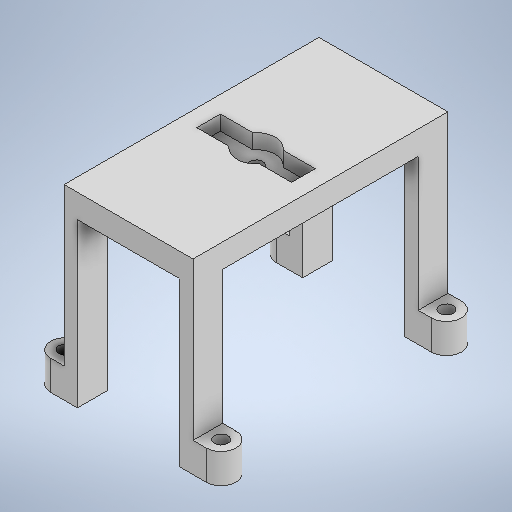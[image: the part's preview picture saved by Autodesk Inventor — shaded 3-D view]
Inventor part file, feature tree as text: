
AUTODESK INVENTOR PART (.ipt)
format: ipt  version: 2025.1 (Build 291241000, 241)  size: 315,392 bytes
history: native  units: in
note: dims shown in document units (in); Inventor stores cm internally (conversion verified against a paired STEP export)
features: extrude x5, sketch x5
ambient origin geometry x8: Origin, YZ Plane, XZ Plane, XY Plane, X Axis, Y Axis, Z Axis, Center Point
bodies: Solid1 (feature_tree)
feature tree (10):
  extrude  "Extrusion1"  Depth=0.3937in
  extrude  "Extrusion2"  Depth=0.3937in
  extrude  "Extrusion3"  Depth=0.3543in
  extrude  "Extrusion4"  Depth=1.7717in TaperAngle=0.0deg
  extrude  "Extrusion5"  Depth=0.315in
  sketch  "Sketch1"  dims[d0=0.3937in d1=0.3937in]
  sketch  "Sketch2"  dims[d2=0.3937in d3=0.3937in]
  sketch  "Sketch3"  dims[d4=0.3543in d5=0.3543in]
  sketch  "Sketch4"  dims[d6=0.3937in d7=0.0in d9=1.7717in d10=0.0in]
  sketch  "Sketch5"  dims[d11=0.315in d12=0.0in d13=0.5118in d14=1.2598in d15=0.315in d16=0.1969in d17=0.0in d18=0.1772in d19=0.315in d20=0.0in]
